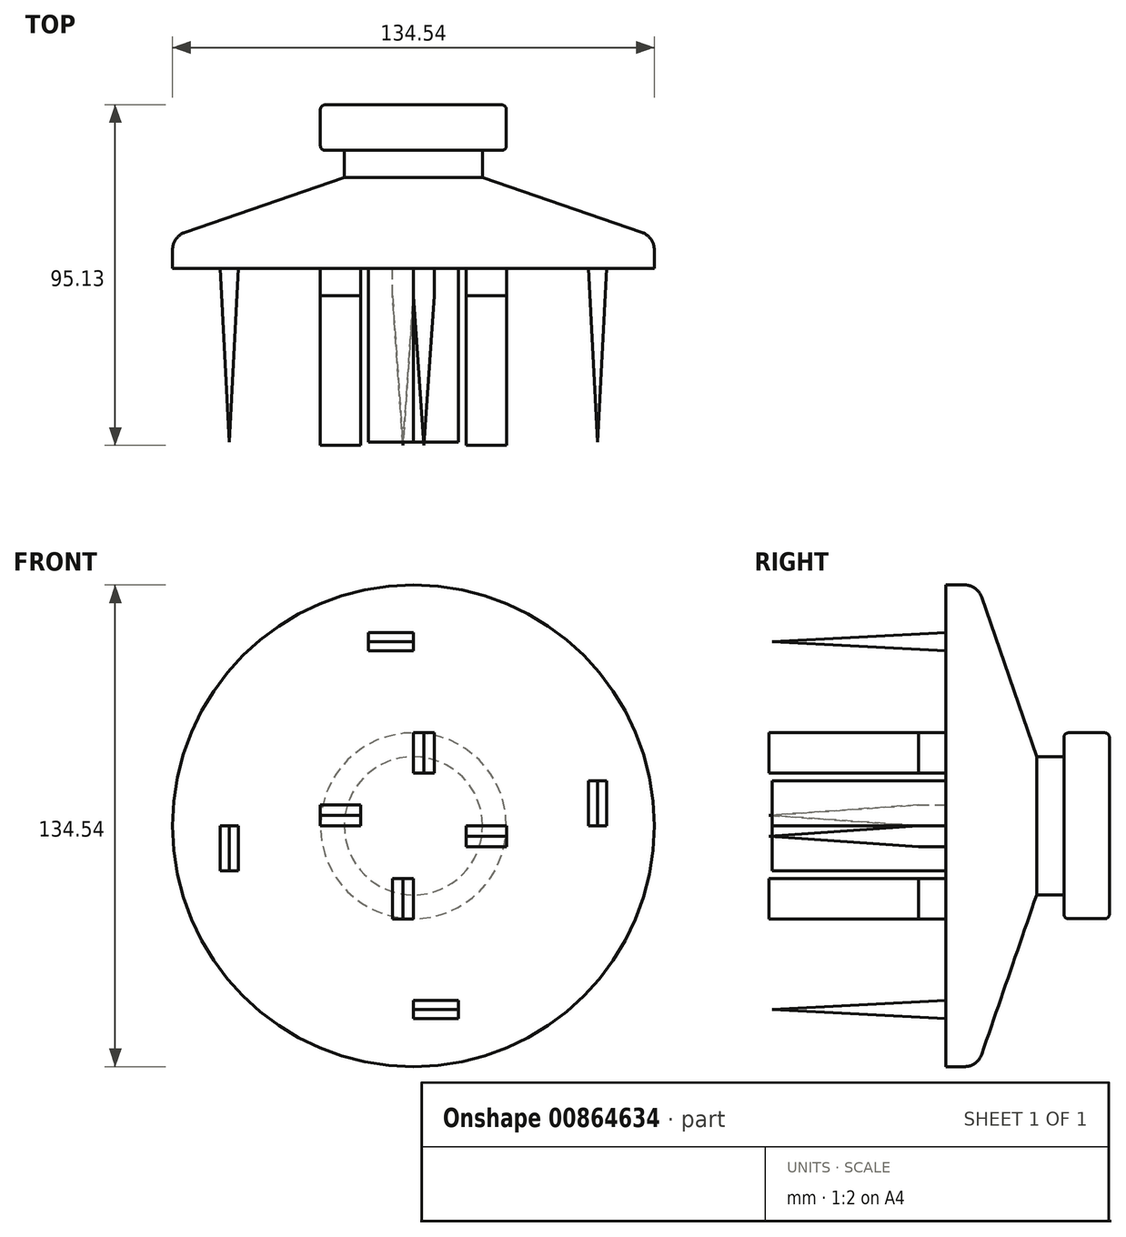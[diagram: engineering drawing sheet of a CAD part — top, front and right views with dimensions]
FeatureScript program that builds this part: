
annotation { "Feature Type Name" : "Feature", "Feature Type Description" : "" }
export const myFeature = defineFeature(function(context is Context, id is Id, definition is map)
    precondition{}
    {
        {
            var Q0;
            Q0=qCreatedBy(makeId("Front.planeOp"),FACE);
            var sketch = newSketch(context, id + "F0", { "sketchPlane" : qUnion([Q0])});
            skCircle(sketch, "E0", {"center": v(0, 0) * mm, "radius": 67.27 * mm});
            skSolve(sketch);
        }
        {
            var Q0;
            Q0=makeQuery(id+"F0.imprint","IMPRINT",FACE,{"disambiguationData":[TD([[makeQuery(id+"F0.imprint","IMPRINT",EDGE,{"derivedFrom":sQuery(id+"F0.wireOp",EDGE,"E0")}),1.0]])]});
            extrude(context, id + "F1", {"entities" : qUnion([Q0]), "oppositeDirection" : true, "depth" : 25.4 * mm, "offsetDistance" : 25.4 * mm});
        }
        {
            var Q0;
            Q0=makeQuery(id+"F1.opExtrude","CAP_EDGE",EDGE,{"disambiguationData":[OSD([sQuery(id+"F0.wireOp",EDGE,"E0")])],"isStart":false});
            chamfer(context, id + "F2", {"entities" : qUnion([Q0]), "chamferType" : ChamferType.OFFSET_ANGLE, "width" : 16.5 * mm, "oppositeDirection" : false, "angle" : 71 * degree, "tangentPropagation" : true});
        }
        {
            var Q0;
            Q0=makeQuery(id+"F1.opExtrude","CAP_FACE",FACE,{"disambiguationData":[OSD([sQuery(id+"F0.wireOp",EDGE,"E0")])],"isStart":false});
            extrude(context, id + "F3", {"entities" : qUnion([Q0]), "operationType" : NewBodyOperationType.ADD, "depth" : 7.62 * mm, "offsetDistance" : 25.4 * mm});
        }
        {
            var Q0;
            Q0=makeQuery(id+"F3.opExtrude","CAP_FACE",FACE,{"disambiguationData":[OSD([sQuery(id+"F0.wireOp",EDGE,"E0")])],"isStart":false});
            var sketch = newSketch(context, id + "F4", { "sketchPlane" : qUnion([Q0])});
            skCircle(sketch, "E1", {"center": v(0, 0) * mm, "radius": 25.97 * mm});
            skSolve(sketch);
        }
        {
            var Q0;
            Q0 = qSketchRegion(id + "F4", true);
            extrude(context, id + "F5", {"entities" : qUnion([Q0]), "operationType" : NewBodyOperationType.ADD, "depth" : 12.7 * mm, "offsetDistance" : 25.4 * mm});
        }
        {
            var Q0;
            Q0=makeQuery(id+"F1.opExtrude","CAP_FACE",FACE,{"disambiguationData":[OSD([sQuery(id+"F0.wireOp",EDGE,"E0")])],"isStart":true});
            var sketch = newSketch(context, id + "F6", { "sketchPlane" : qUnion([Q0])});
            skLineSegment(sketch, "E2.bottom", {"start": v(-12.55, 48.84) * mm, "end": v(0, 48.84) * mm});
            skLineSegment(sketch, "E2.top", {"start": v(-12.55, 53.92) * mm, "end": v(0, 53.92) * mm});
            skLineSegment(sketch, "E2.left", {"start": v(-12.55, 48.84) * mm, "end": v(-12.55, 53.92) * mm});
            skLineSegment(sketch, "E2.right", {"start": v(0, 48.84) * mm, "end": v(0, 53.92) * mm});
            skLineSegment(sketch, "E3.bottom", {"start": v(0, 14.71) * mm, "end": v(5.84, 14.71) * mm});
            skLineSegment(sketch, "E3.top", {"start": v(0, 26.09) * mm, "end": v(5.84, 26.09) * mm});
            skLineSegment(sketch, "E3.left", {"start": v(0, 14.71) * mm, "end": v(0, 26.09) * mm});
            skLineSegment(sketch, "E3.right", {"start": v(5.84, 14.71) * mm, "end": v(5.84, 26.09) * mm});
            skLineSegment(sketch, "E4.1.0", {"start": v(-53.92, -12.55) * mm, "end": v(-53.92, 0) * mm});
            skLineSegment(sketch, "E4.1.1", {"start": v(-48.84, -12.55) * mm, "end": v(-53.92, -12.55) * mm});
            skLineSegment(sketch, "E4.1.2", {"start": v(-48.84, -12.55) * mm, "end": v(-48.84, 0) * mm});
            skLineSegment(sketch, "E4.1.3", {"start": v(-48.84, 0) * mm, "end": v(-53.92, 0) * mm});
            skLineSegment(sketch, "E4.1.4", {"start": v(-26.09, 0) * mm, "end": v(-26.09, 5.84) * mm});
            skLineSegment(sketch, "E4.1.5", {"start": v(-14.71, 0) * mm, "end": v(-26.09, 0) * mm});
            skLineSegment(sketch, "E4.1.6", {"start": v(-14.71, 0) * mm, "end": v(-14.71, 5.84) * mm});
            skLineSegment(sketch, "E4.1.7", {"start": v(-14.71, 5.84) * mm, "end": v(-26.09, 5.84) * mm});
            skLineSegment(sketch, "E4.2.0", {"start": v(12.55, -53.92) * mm, "end": v(0, -53.92) * mm});
            skLineSegment(sketch, "E4.2.1", {"start": v(12.55, -48.84) * mm, "end": v(12.55, -53.92) * mm});
            skLineSegment(sketch, "E4.2.2", {"start": v(12.55, -48.84) * mm, "end": v(0, -48.84) * mm});
            skLineSegment(sketch, "E4.2.3", {"start": v(0, -48.84) * mm, "end": v(0, -53.92) * mm});
            skLineSegment(sketch, "E4.2.4", {"start": v(0, -26.09) * mm, "end": v(-5.84, -26.09) * mm});
            skLineSegment(sketch, "E4.2.5", {"start": v(0, -14.71) * mm, "end": v(0, -26.09) * mm});
            skLineSegment(sketch, "E4.2.6", {"start": v(0, -14.71) * mm, "end": v(-5.84, -14.71) * mm});
            skLineSegment(sketch, "E4.2.7", {"start": v(-5.84, -14.71) * mm, "end": v(-5.84, -26.09) * mm});
            skLineSegment(sketch, "E4.3.0", {"start": v(53.92, 12.55) * mm, "end": v(53.92, 0) * mm});
            skLineSegment(sketch, "E4.3.1", {"start": v(48.84, 12.55) * mm, "end": v(53.92, 12.55) * mm});
            skLineSegment(sketch, "E4.3.2", {"start": v(48.84, 12.55) * mm, "end": v(48.84, 0) * mm});
            skLineSegment(sketch, "E4.3.3", {"start": v(48.84, 0) * mm, "end": v(53.92, 0) * mm});
            skLineSegment(sketch, "E4.3.4", {"start": v(26.09, 0) * mm, "end": v(26.09, -5.84) * mm});
            skLineSegment(sketch, "E4.3.5", {"start": v(14.71, 0) * mm, "end": v(26.09, 0) * mm});
            skLineSegment(sketch, "E4.3.6", {"start": v(14.71, 0) * mm, "end": v(14.71, -5.84) * mm});
            skLineSegment(sketch, "E4.3.7", {"start": v(14.71, -5.84) * mm, "end": v(26.09, -5.84) * mm});
            skPoint(sketch, "E4.center", {"position": v(0, 0) * mm});
            skSolve(sketch);
        }
        {
            var Q0;
            Q0 = qSketchRegion(id + "F6", true);
            extrude(context, id + "F7", {"entities" : qUnion([Q0]), "operationType" : NewBodyOperationType.ADD, "depth" : 50.8 * mm, "offsetDistance" : 25.4 * mm});
        }
        {
            var Q0;
            Q0=makeQuery(id+"F7.opExtrude","CAP_EDGE",EDGE,{"disambiguationData":[OSD([sQuery(id+"F6.wireOp",EDGE,"E2.top")])],"isStart":false});
            var Q1;
            Q1=makeQuery(id+"F7.opExtrude","CAP_EDGE",EDGE,{"disambiguationData":[OSD([sQuery(id+"F6.wireOp",EDGE,"E2.bottom")])],"isStart":false});
            chamfer(context, id + "F8", {"entities" : qUnion([Q0, Q1]), "chamferType" : ChamferType.OFFSET_ANGLE, "width" : 50.8 * mm, "oppositeDirection" : false, "angle" : 3 * degree, "tangentPropagation" : true});
        }
        {
            var Q0;
            Q0=makeQuery(id+"F7.opExtrude","CAP_EDGE",EDGE,{"disambiguationData":[OSD([sQuery(id+"F6.wireOp",EDGE,"E3.right")])],"isStart":false});
            var Q1;
            Q1=makeQuery(id+"F7.opExtrude","CAP_EDGE",EDGE,{"disambiguationData":[OSD([sQuery(id+"F6.wireOp",EDGE,"E3.left")])],"isStart":false});
            chamfer(context, id + "F9", {"entities" : qUnion([Q0, Q1]), "chamferType" : ChamferType.OFFSET_ANGLE, "width" : 43.18 * mm, "oppositeDirection" : true, "angle" : 4 * degree, "tangentPropagation" : true});
        }
        {
            var Q0;
            Q0=makeQuery(id+"F7.opExtrude","CAP_EDGE",EDGE,{"disambiguationData":[OSD([sQuery(id+"F6.wireOp",EDGE,"E4.1.5")])],"isStart":false});
            var Q1;
            Q1=makeQuery(id+"F7.opExtrude","CAP_EDGE",EDGE,{"disambiguationData":[OSD([sQuery(id+"F6.wireOp",EDGE,"E4.1.7")])],"isStart":false});
            chamfer(context, id + "F10", {"entities" : qUnion([Q0, Q1]), "chamferType" : ChamferType.OFFSET_ANGLE, "width" : 43.18 * mm, "oppositeDirection" : false, "angle" : 4 * degree, "tangentPropagation" : true});
        }
        {
            var Q0;
            Q0=makeQuery(id+"F7.opExtrude","CAP_EDGE",EDGE,{"disambiguationData":[OSD([sQuery(id+"F6.wireOp",EDGE,"E4.2.7")])],"isStart":false});
            var Q1;
            Q1=makeQuery(id+"F7.opExtrude","CAP_EDGE",EDGE,{"disambiguationData":[OSD([sQuery(id+"F6.wireOp",EDGE,"E4.2.5")])],"isStart":false});
            chamfer(context, id + "F11", {"entities" : qUnion([Q0, Q1]), "chamferType" : ChamferType.OFFSET_ANGLE, "width" : 43.18 * mm, "oppositeDirection" : true, "angle" : 4 * degree, "tangentPropagation" : true});
        }
        {
            var Q0;
            Q0=makeQuery(id+"F7.opExtrude","CAP_EDGE",EDGE,{"disambiguationData":[OSD([sQuery(id+"F6.wireOp",EDGE,"E4.3.7")])],"isStart":false});
            var Q1;
            Q1=makeQuery(id+"F7.opExtrude","CAP_EDGE",EDGE,{"disambiguationData":[OSD([sQuery(id+"F6.wireOp",EDGE,"E4.3.5")])],"isStart":false});
            chamfer(context, id + "F12", {"entities" : qUnion([Q0, Q1]), "chamferType" : ChamferType.OFFSET_ANGLE, "width" : 43.18 * mm, "oppositeDirection" : true, "angle" : 4 * degree, "tangentPropagation" : true});
        }
        {
            var Q0;
            Q0=makeQuery(id+"F7.opExtrude","CAP_EDGE",EDGE,{"disambiguationData":[OSD([sQuery(id+"F6.wireOp",EDGE,"E4.1.2")])],"isStart":false});
            var Q1;
            Q1=makeQuery(id+"F7.opExtrude","CAP_EDGE",EDGE,{"disambiguationData":[OSD([sQuery(id+"F6.wireOp",EDGE,"E4.1.0")])],"isStart":false});
            chamfer(context, id + "F13", {"entities" : qUnion([Q0, Q1]), "chamferType" : ChamferType.OFFSET_ANGLE, "width" : 50.8 * mm, "oppositeDirection" : true, "angle" : 3 * degree, "tangentPropagation" : true});
        }
        {
            var Q0;
            Q0=makeQuery(id+"F7.opExtrude","CAP_EDGE",EDGE,{"disambiguationData":[OSD([sQuery(id+"F6.wireOp",EDGE,"E4.2.0")])],"isStart":false});
            var Q1;
            Q1=makeQuery(id+"F7.opExtrude","CAP_EDGE",EDGE,{"disambiguationData":[OSD([sQuery(id+"F6.wireOp",EDGE,"E4.2.2")])],"isStart":false});
            chamfer(context, id + "F14", {"entities" : qUnion([Q0, Q1]), "chamferType" : ChamferType.OFFSET_ANGLE, "width" : 50.8 * mm, "oppositeDirection" : false, "angle" : 3 * degree, "tangentPropagation" : true});
        }
        {
            var Q0;
            Q0=makeQuery(id+"F7.opExtrude","CAP_EDGE",EDGE,{"disambiguationData":[OSD([sQuery(id+"F6.wireOp",EDGE,"E4.3.0")])],"isStart":false});
            var Q1;
            Q1=makeQuery(id+"F7.opExtrude","CAP_EDGE",EDGE,{"disambiguationData":[OSD([sQuery(id+"F6.wireOp",EDGE,"E4.3.2")])],"isStart":false});
            chamfer(context, id + "F15", {"entities" : qUnion([Q0, Q1]), "chamferType" : ChamferType.OFFSET_ANGLE, "width" : 50.8 * mm, "oppositeDirection" : false, "angle" : 3 * degree, "tangentPropagation" : true});
        }
        {
            var Q0;
            {var subQ0=sQuery(id+"F0.wireOp",EDGE,"E0");Q0=makeQuery(id+"F2.opChamfer","BLEND_EDGE",EDGE,{"blendedFrom":[makeQuery(id+"F1.opExtrude","CAP_EDGE",EDGE,{"disambiguationData":[OSD([subQ0])],"isStart":false}),makeQuery(id+"F1.opExtrude","SWEPT_FACE",FACE,{"disambiguationData":[OSD([subQ0])]})],"blendedInto":[makeQuery(id+"F1.opExtrude","SWEPT_FACE",FACE,{"disambiguationData":[OSD([subQ0])]})]});}
            fillet(context, id + "F16", {"entities" : qUnion([Q0]), "radius" : 5.08 * mm, "tangentPropagation" : true, "allowEdgeOverflow" : false});
        }
        {
            var Q0;
            Q0=makeQuery(id+"F5.opExtrude","CAP_EDGE",EDGE,{"disambiguationData":[OSD([sQuery(id+"F4.wireOp",EDGE,"E1")])],"isStart":false});
            var Q1;
            Q1=makeQuery(id+"F5.opExtrude","CAP_EDGE",EDGE,{"disambiguationData":[OSD([sQuery(id+"F4.wireOp",EDGE,"E1")])],"isStart":true});
            fillet(context, id + "F17", {"entities" : qUnion([Q0, Q1]), "radius" : 1.27 * mm, "tangentPropagation" : true, "allowEdgeOverflow" : false});
        }
    });
